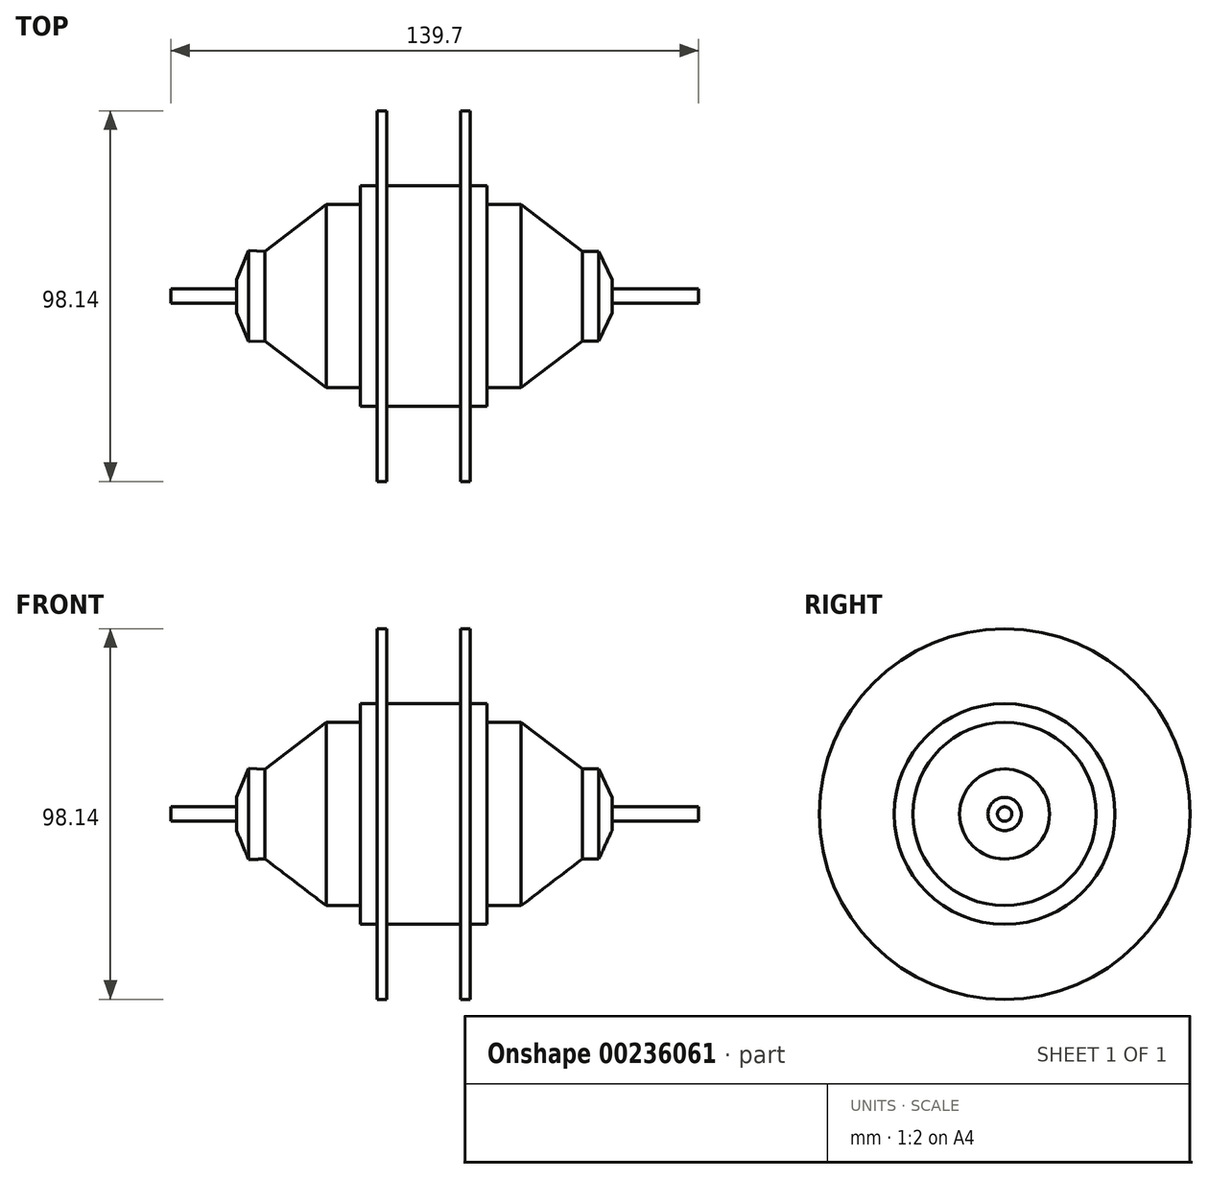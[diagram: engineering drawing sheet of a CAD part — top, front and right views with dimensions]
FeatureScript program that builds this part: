
annotation { "Feature Type Name" : "Feature", "Feature Type Description" : "" }
export const myFeature = defineFeature(function(context is Context, id is Id, definition is map)
    precondition{}
    {
        {
            var Q0;
            Q0=qCreatedBy(makeId("Top.planeOp"),FACE);
            var sketch = newSketch(context, id + "F0", { "sketchPlane" : qUnion([Q0])});
            skLineSegment(sketch, "E0", {"start": v(-16.03, 24.26) * mm, "end": v(-7, 24.26) * mm});
            skLineSegment(sketch, "E1", {"start": v(-7, 24.26) * mm, "end": v(-7, 29.22) * mm});
            skLineSegment(sketch, "E2", {"start": v(-7, 29.22) * mm, "end": v(-2.5, 29.22) * mm});
            skLineSegment(sketch, "E3", {"start": v(-2.5, 29.22) * mm, "end": v(-2.5, 49.07) * mm});
            skLineSegment(sketch, "E4", {"start": v(-2.5, 49.07) * mm, "end": v(0, 49.07) * mm});
            skLineSegment(sketch, "E5", {"start": v(0, 49.07) * mm, "end": v(0, 29.22) * mm});
            skLineSegment(sketch, "E6", {"start": v(0, 29.22) * mm, "end": v(19.6, 29.22) * mm});
            skLineSegment(sketch, "E7", {"start": v(19.6, 29.22) * mm, "end": v(19.6, 49.07) * mm});
            skLineSegment(sketch, "E8", {"start": v(19.6, 49.07) * mm, "end": v(22.1, 49.07) * mm});
            skLineSegment(sketch, "E9", {"start": v(22.1, 49.07) * mm, "end": v(22.1, 29.22) * mm});
            skLineSegment(sketch, "E10", {"start": v(22.1, 29.22) * mm, "end": v(26.6, 29.22) * mm});
            skLineSegment(sketch, "E11", {"start": v(26.6, 29.22) * mm, "end": v(26.6, 24.26) * mm});
            skLineSegment(sketch, "E12", {"start": v(26.6, 24.26) * mm, "end": v(35.63, 24.26) * mm});
            skLineSegment(sketch, "E13", {"start": v(59.66, 0) * mm, "end": v(-35.6, 0) * mm});
            skLineSegment(sketch, "E14", {"start": v(35.63, 24.26) * mm, "end": v(51.81, 11.9) * mm});
            skLineSegment(sketch, "E15", {"start": v(51.81, 11.9) * mm, "end": v(56.17, 11.9) * mm});
            skLineSegment(sketch, "E16", {"start": v(56.17, 11.9) * mm, "end": v(59.66, 4.41) * mm});
            skLineSegment(sketch, "E17", {"start": v(59.66, 4.41) * mm, "end": v(59.66, 0) * mm});
            skLineSegment(sketch, "E18", {"start": v(-16.03, 24.26) * mm, "end": v(-32.2, 11.9) * mm});
            skLineSegment(sketch, "E19", {"start": v(-32.2, 11.9) * mm, "end": v(-36.56, 12.08) * mm});
            skLineSegment(sketch, "E20", {"start": v(-35.6, 0) * mm, "end": v(-39.7, 0) * mm});
            skLineSegment(sketch, "E21", {"start": v(-36.56, 12.08) * mm, "end": v(-39.7, 4.43) * mm});
            skLineSegment(sketch, "E22", {"start": v(-39.7, 4.43) * mm, "end": v(-39.7, 0) * mm});
            skSolve(sketch);
        }
        {
            var Q0;
            Q0=qCreatedBy(makeId("Right.planeOp"),FACE);
            var sketch = newSketch(context, id + "F1", { "sketchPlane" : qUnion([Q0])});
            skCircle(sketch, "E23", {"center": v(0, 0) * mm, "radius": 1.9 * mm});
            skSolve(sketch);
        }
        {
            var Q0;
            Q0 = qSketchRegion(id + "F1", true);
            extrude(context, id + "F2", {"entities" : qUnion([Q0]), "depth" : 82.55 * mm, "hasSecondDirection" : true, "secondDirectionOppositeDirection" : true, "secondDirectionDepth" : 57.15 * mm});
        }
        {
            var Q0;
            Q0 = qSketchRegion(id + "F1", true);
            extrude(context, id + "F3", {"entities" : qUnion([Q0]), "operationType" : NewBodyOperationType.ADD, "depth" : 0.76 * mm});
        }
        {
            var Q0;
            Q0 = qSketchRegion(id + "F0", true);
            var Q1;
            Q1=makeQuery(id+"F2.opExtrude","SWEPT_FACE",FACE,{"disambiguationData":[OSD([sQuery(id+"F1.wireOp",EDGE,"E23")])]});
            revolve(context, id + "F4", {"operationType" : NewBodyOperationType.ADD, "entities" : qUnion([Q0]), "axis" : qUnion([Q1]), "revolveType" : RevolveType.FULL});
        }
    });
